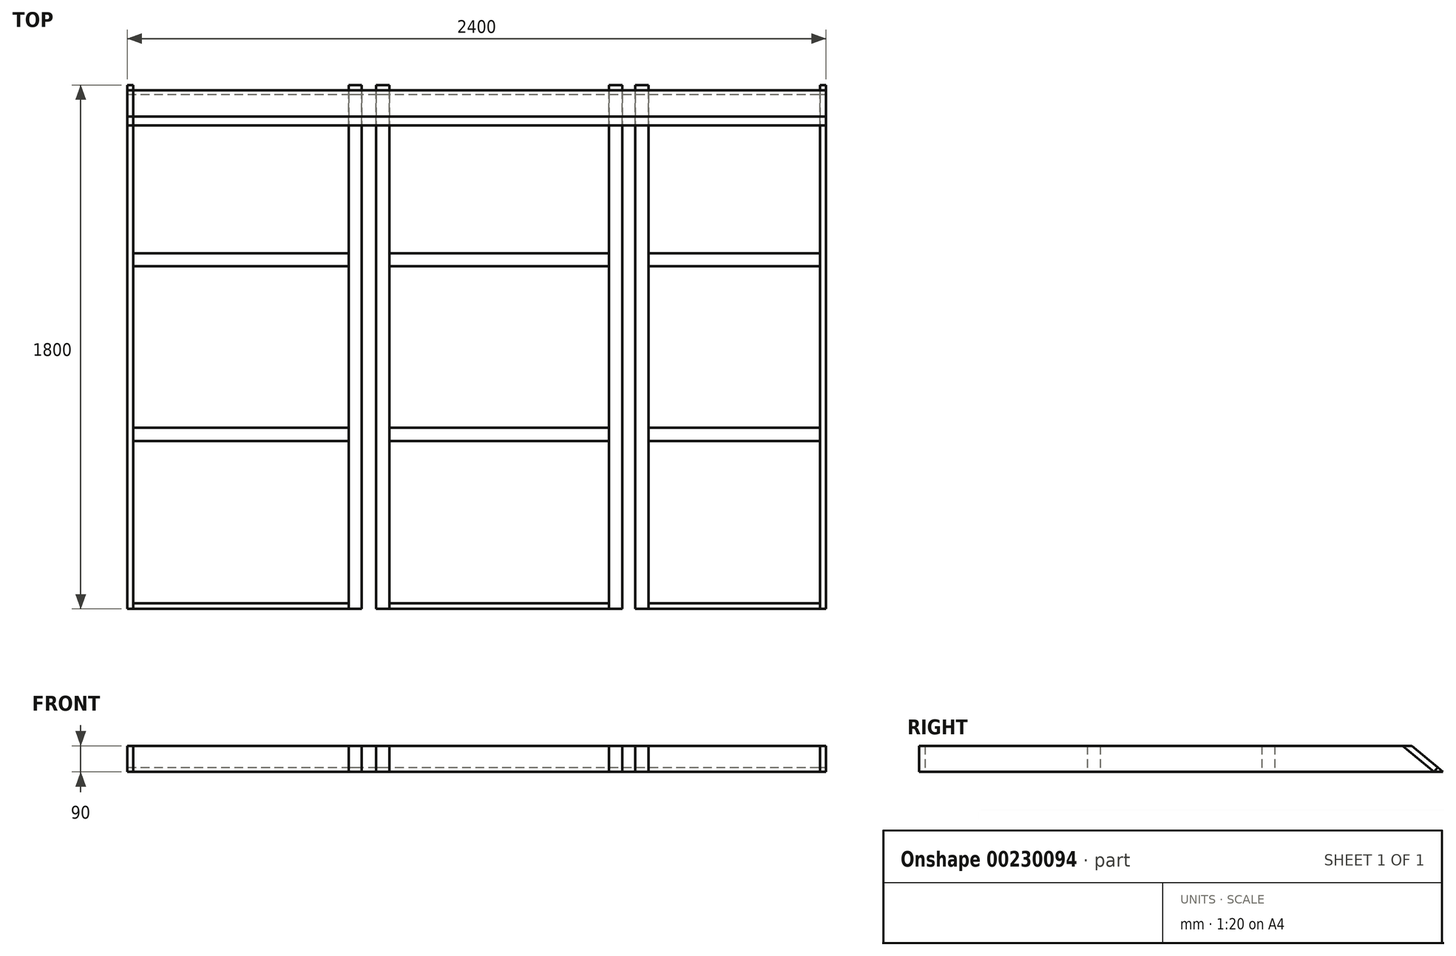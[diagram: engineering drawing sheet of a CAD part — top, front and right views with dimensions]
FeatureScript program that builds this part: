
annotation { "Feature Type Name" : "Feature", "Feature Type Description" : "" }
export const myFeature = defineFeature(function(context is Context, id is Id, definition is map)
    precondition{}
    {
        {
            var Q0;
            Q0=qCreatedBy(makeId("Top.planeOp"),FACE);
            var sketch = newSketch(context, id + "F0", { "sketchPlane" : qUnion([Q0])});
            skLineSegment(sketch, "E0.bottom", {"start": v(1200, 900) * mm, "end": v(-1200, 900) * mm});
            skLineSegment(sketch, "E0.top", {"start": v(1200, -900) * mm, "end": v(-1200, -900) * mm});
            skLineSegment(sketch, "E0.left", {"start": v(1200, 900) * mm, "end": v(1200, -900) * mm});
            skLineSegment(sketch, "E0.right", {"start": v(-1200, 900) * mm, "end": v(-1200, -900) * mm});
            skPoint(sketch, "E0.middle", {"position": v(0, 0) * mm});
            skLineSegment(sketch, "E1", {"start": v(-1180, 900) * mm, "end": v(-1180, -900) * mm});
            skLineSegment(sketch, "E2", {"start": v(-440, 900) * mm, "end": v(-440, -900) * mm});
            skLineSegment(sketch, "E3", {"start": v(-395, 900) * mm, "end": v(-395, -900) * mm});
            skLineSegment(sketch, "E4", {"start": v(-345, 900) * mm, "end": v(-345, -900) * mm});
            skLineSegment(sketch, "E5", {"start": v(-300, 900) * mm, "end": v(-300, -900) * mm});
            skPoint(sketch, "E6.middle", {"position": v(666.84, 0) * mm});
            skLineSegment(sketch, "E7", {"start": v(455, 900) * mm, "end": v(455, -900) * mm});
            skLineSegment(sketch, "E8", {"start": v(500, 900) * mm, "end": v(500, -900) * mm});
            skLineSegment(sketch, "E9", {"start": v(545, 900) * mm, "end": v(545, -900) * mm});
            skLineSegment(sketch, "E10", {"start": v(590, 900) * mm, "end": v(590, -900) * mm});
            skLineSegment(sketch, "E11", {"start": v(1180, 900) * mm, "end": v(1180, -900) * mm});
            skLineSegment(sketch, "E12", {"start": v(-1180, -880) * mm, "end": v(-440, -880) * mm});
            skLineSegment(sketch, "E13", {"start": v(-300, -880) * mm, "end": v(455, -880) * mm});
            skLineSegment(sketch, "E14", {"start": v(590, -880) * mm, "end": v(1180, -880) * mm});
            skLineSegment(sketch, "E15", {"start": v(-1200, 900) * mm, "end": v(-1457.4, 900) * mm});
            skLineSegment(sketch, "E16", {"start": v(-1457.4, 900) * mm, "end": v(-1457.4, 300) * mm});
            skLineSegment(sketch, "E17", {"start": v(-1457.4, 300) * mm, "end": v(-1457.4, -300) * mm});
            skLineSegment(sketch, "E18", {"start": v(-1457.4, -300) * mm, "end": v(-1457.4, -900) * mm});
            skLineSegment(sketch, "E19", {"start": v(-1457.4, 300) * mm, "end": v(1566.79, 300) * mm, "construction": true});
            skLineSegment(sketch, "E20", {"start": v(-1457.4, -300) * mm, "end": v(1566.79, -300) * mm, "construction": true});
            skLineSegment(sketch, "E21", {"start": v(0, 900) * mm, "end": v(0, -1083.47) * mm, "construction": true});
            skLineSegment(sketch, "E22.bottom", {"start": v(1180, 277.5) * mm, "end": v(590, 277.5) * mm});
            skLineSegment(sketch, "E22.top", {"start": v(1180, 322.5) * mm, "end": v(590, 322.5) * mm});
            skLineSegment(sketch, "E22.left", {"start": v(1180, 277.5) * mm, "end": v(1180, 322.5) * mm});
            skLineSegment(sketch, "E22.right", {"start": v(-1180, 277.5) * mm, "end": v(-1180, 322.5) * mm});
            skPoint(sketch, "E22.middle", {"position": v(0, 300) * mm});
            skLineSegment(sketch, "E23.bottom", {"start": v(1180, -322.5) * mm, "end": v(590, -322.5) * mm});
            skLineSegment(sketch, "E23.top", {"start": v(1180, -277.5) * mm, "end": v(590, -277.5) * mm});
            skLineSegment(sketch, "E23.left", {"start": v(1180, -322.5) * mm, "end": v(1180, -277.5) * mm});
            skLineSegment(sketch, "E23.right", {"start": v(-1180, -322.5) * mm, "end": v(-1180, -277.5) * mm});
            skPoint(sketch, "E23.middle", {"position": v(0, -300) * mm});
            skLineSegment(sketch, "E24.trimOffspring", {"start": v(-440, -322.5) * mm, "end": v(-1180, -322.5) * mm});
            skLineSegment(sketch, "E25.trimOffspring", {"start": v(-440, -277.5) * mm, "end": v(-1180, -277.5) * mm});
            skLineSegment(sketch, "E26.trimOffspring", {"start": v(-440, 322.5) * mm, "end": v(-1180, 322.5) * mm});
            skLineSegment(sketch, "E27.trimOffspring", {"start": v(-440, 277.5) * mm, "end": v(-1180, 277.5) * mm});
            skLineSegment(sketch, "E28.trimOffspring", {"start": v(455, 322.5) * mm, "end": v(-300, 322.5) * mm});
            skLineSegment(sketch, "E29.trimOffspring", {"start": v(455, 277.5) * mm, "end": v(-300, 277.5) * mm});
            skLineSegment(sketch, "E30.trimOffspring", {"start": v(455, -277.5) * mm, "end": v(-300, -277.5) * mm});
            skLineSegment(sketch, "E31.trimOffspring", {"start": v(455, -322.5) * mm, "end": v(-300, -322.5) * mm});
            skLineSegment(sketch, "E32", {"start": v(-440, 900) * mm, "end": v(-395, 900) * mm});
            skLineSegment(sketch, "E33", {"start": v(-345, 900) * mm, "end": v(-300, 900) * mm});
            skLineSegment(sketch, "E34", {"start": v(455, 900) * mm, "end": v(500, 900) * mm});
            skLineSegment(sketch, "E35", {"start": v(545, 900) * mm, "end": v(590, 900) * mm});
            skSolve(sketch);
        }
        {
            var Q0;
            {var subQ0=sQuery(id+"F0.wireOp",EDGE,"E0.right");Q0=makeQuery(id+"F0.imprint","IMPRINT",FACE,{"disambiguationData":[TD([[makeQuery(id+"F0.imprint","IMPRINT",EDGE,{"derivedFrom":subQ0}),1.0]])]});}
            var Q1;
            {var subQ6=sQuery(id+"F0.wireOp",EDGE,"E3");Q1=makeQuery(id+"F0.imprint","IMPRINT",FACE,{"disambiguationData":[TD([[makeQuery(id+"F0.imprint","IMPRINT",EDGE,{"derivedFrom":subQ6}),-1.0]])]});}
            var Q2;
            {var subQ4=sQuery(id+"F0.wireOp",EDGE,"E4");Q2=makeQuery(id+"F0.imprint","IMPRINT",FACE,{"disambiguationData":[TD([[makeQuery(id+"F0.imprint","IMPRINT",EDGE,{"derivedFrom":subQ4}),1.0]])]});}
            var Q3;
            {var subQ6=sQuery(id+"F0.wireOp",EDGE,"E8");Q3=makeQuery(id+"F0.imprint","IMPRINT",FACE,{"disambiguationData":[TD([[makeQuery(id+"F0.imprint","IMPRINT",EDGE,{"derivedFrom":subQ6}),-1.0]])]});}
            var Q4;
            {var subQ4=sQuery(id+"F0.wireOp",EDGE,"E9");Q4=makeQuery(id+"F0.imprint","IMPRINT",FACE,{"disambiguationData":[TD([[makeQuery(id+"F0.imprint","IMPRINT",EDGE,{"derivedFrom":subQ4}),1.0]])]});}
            var Q5;
            {var subQ4=sQuery(id+"F0.wireOp",EDGE,"E0.left");Q5=makeQuery(id+"F0.imprint","IMPRINT",FACE,{"disambiguationData":[TD([[makeQuery(id+"F0.imprint","IMPRINT",EDGE,{"derivedFrom":subQ4}),-1.0]])]});}
            extrude(context, id + "F1", {"entities" : qUnion([Q0, Q1, Q2, Q3, Q4, Q5]), "depth" : 90 * mm, "offsetDistance" : 25 * mm});
        }
        {
            var Q0;
            {var subQ5=sQuery(id+"F0.wireOp",EDGE,"E12");Q0=makeQuery(id+"F0.imprint","IMPRINT",FACE,{"disambiguationData":[TD([[makeQuery(id+"F0.imprint","IMPRINT",EDGE,{"derivedFrom":subQ5}),-1.0]])]});}
            var Q1;
            {var subQ5=sQuery(id+"F0.wireOp",EDGE,"E13");Q1=makeQuery(id+"F0.imprint","IMPRINT",FACE,{"disambiguationData":[TD([[makeQuery(id+"F0.imprint","IMPRINT",EDGE,{"derivedFrom":subQ5}),-1.0]])]});}
            var Q2;
            {var subQ5=sQuery(id+"F0.wireOp",EDGE,"E14");Q2=makeQuery(id+"F0.imprint","IMPRINT",FACE,{"disambiguationData":[TD([[makeQuery(id+"F0.imprint","IMPRINT",EDGE,{"derivedFrom":subQ5}),-1.0]])]});}
            extrude(context, id + "F2", {"entities" : qUnion([Q0, Q1, Q2]), "depth" : 90 * mm, "offsetDistance" : 25 * mm});
        }
        {
            var Q0;
            {var subQ0=sQuery(id+"F0.wireOp",EDGE,"E26.trimOffspring");Q0=makeQuery(id+"F0.imprint","IMPRINT",FACE,{"disambiguationData":[TD([[makeQuery(id+"F0.imprint","IMPRINT",EDGE,{"derivedFrom":subQ0}),1.0]])]});}
            var Q1;
            {var subQ0=sQuery(id+"F0.wireOp",EDGE,"E28.trimOffspring");Q1=makeQuery(id+"F0.imprint","IMPRINT",FACE,{"disambiguationData":[TD([[makeQuery(id+"F0.imprint","IMPRINT",EDGE,{"derivedFrom":subQ0}),1.0]])]});}
            var Q2;
            {var subQ0=sQuery(id+"F0.wireOp",EDGE,"E22.bottom");Q2=makeQuery(id+"F0.imprint","IMPRINT",FACE,{"disambiguationData":[TD([[makeQuery(id+"F0.imprint","IMPRINT",EDGE,{"derivedFrom":subQ0}),-1.0]])]});}
            var Q3;
            {var subQ0=sQuery(id+"F0.wireOp",EDGE,"E23.bottom");Q3=makeQuery(id+"F0.imprint","IMPRINT",FACE,{"disambiguationData":[TD([[makeQuery(id+"F0.imprint","IMPRINT",EDGE,{"derivedFrom":subQ0}),-1.0]])]});}
            var Q4;
            {var subQ0=sQuery(id+"F0.wireOp",EDGE,"E24.trimOffspring");Q4=makeQuery(id+"F0.imprint","IMPRINT",FACE,{"disambiguationData":[TD([[makeQuery(id+"F0.imprint","IMPRINT",EDGE,{"derivedFrom":subQ0}),-1.0]])]});}
            var Q5;
            {var subQ0=sQuery(id+"F0.wireOp",EDGE,"E30.trimOffspring");Q5=makeQuery(id+"F0.imprint","IMPRINT",FACE,{"disambiguationData":[TD([[makeQuery(id+"F0.imprint","IMPRINT",EDGE,{"derivedFrom":subQ0}),1.0]])]});}
            extrude(context, id + "F3", {"entities" : qUnion([Q0, Q1, Q2, Q3, Q4, Q5]), "depth" : 90 * mm, "offsetDistance" : 25 * mm});
        }
        {
            var Q0;
            Q0=makeQuery(id+"F1.opExtrude","SWEPT_FACE",FACE,{"disambiguationData":[OSD([sQuery(id+"F0.wireOp",EDGE,"E0.left")])]});
            var sketch = newSketch(context, id + "F4", { "sketchPlane" : qUnion([Q0])});
            skLineSegment(sketch, "E36", {"start": v(900, 0) * mm, "end": v(900, 90) * mm});
            skLineSegment(sketch, "E37", {"start": v(900, 0) * mm, "end": v(792.74, 90) * mm});
            skLineSegment(sketch, "E38", {"start": v(761.63, 90) * mm, "end": v(868.89, 0) * mm});
            skLineSegment(sketch, "E39", {"start": v(792.74, 90) * mm, "end": v(779.89, 74.68) * mm});
            skLineSegment(sketch, "E40", {"start": v(868.89, 0) * mm, "end": v(881.74, 15.32) * mm});
            skLineSegment(sketch, "E41", {"start": v(868.89, 0) * mm, "end": v(798.88, 0) * mm});
            skLineSegment(sketch, "E42", {"start": v(798.88, 0) * mm, "end": v(784.8, 11.8) * mm});
            skLineSegment(sketch, "E43", {"start": v(784.8, 11.8) * mm, "end": v(813.73, 46.28) * mm});
            skLineSegment(sketch, "E44.bottom", {"start": v(971.7, 98.75) * mm, "end": v(1016.7, 98.75) * mm});
            skLineSegment(sketch, "E44.top", {"start": v(971.7, 8.75) * mm, "end": v(1016.7, 8.75) * mm});
            skLineSegment(sketch, "E44.left", {"start": v(971.7, 98.75) * mm, "end": v(971.7, 8.75) * mm});
            skLineSegment(sketch, "E44.right", {"start": v(1016.7, 98.75) * mm, "end": v(1016.7, 8.75) * mm});
            skLineSegment(sketch, "E45", {"start": v(955.44, 99.95) * mm, "end": v(1030.31, 10.72) * mm});
            skLineSegment(sketch, "E46", {"start": v(994.2, 98.75) * mm, "end": v(994.2, 8.75) * mm, "construction": true});
            skLineSegment(sketch, "E47", {"start": v(1016.7, 53.75) * mm, "end": v(971.7, 53.75) * mm, "construction": true});
            skPoint(sketch, "E48", {"position": v(994.2, 53.75) * mm});
            skPoint(sketch, "E49", {"position": v(1016.7, 26.93) * mm});
            skPoint(sketch, "E50", {"position": v(971.7, 80.56) * mm});
            skLineSegment(sketch, "E51", {"start": v(1092.55, 162.61) * mm, "end": v(1326.88, 162.61) * mm});
            skLineSegment(sketch, "E52", {"start": v(1233.6, 162.61) * mm, "end": v(1147.43, 90.3) * mm});
            skLineSegment(sketch, "E53", {"start": v(1164.65, 104.76) * mm, "end": v(1135.73, 139.23) * mm});
            skLineSegment(sketch, "E54", {"start": v(1135.73, 139.23) * mm, "end": v(1204.67, 197.08) * mm});
            skLineSegment(sketch, "E55", {"start": v(1204.67, 197.08) * mm, "end": v(1233.6, 162.61) * mm});
            skLineSegment(sketch, "E56.bottom", {"start": v(1498.29, 50.73) * mm, "end": v(1543.29, 50.73) * mm});
            skLineSegment(sketch, "E56.top", {"start": v(1498.29, 140.73) * mm, "end": v(1543.29, 140.73) * mm});
            skLineSegment(sketch, "E56.left", {"start": v(1498.29, 50.73) * mm, "end": v(1498.29, 140.73) * mm});
            skLineSegment(sketch, "E56.right", {"start": v(1543.29, 50.73) * mm, "end": v(1543.29, 140.73) * mm});
            skLineSegment(sketch, "E57", {"start": v(1558.5, 140.67) * mm, "end": v(1483.63, 51.45) * mm});
            skLineSegment(sketch, "E58", {"start": v(1498.29, 95.73) * mm, "end": v(1543.29, 95.73) * mm});
            skPoint(sketch, "E59", {"position": v(1520.79, 95.73) * mm});
            skLineSegment(sketch, "E60", {"start": v(900, 0) * mm, "end": v(991.3, -76.6) * mm, "construction": true});
            skLineSegment(sketch, "E61", {"start": v(900, 0) * mm, "end": v(869.84, -82.85) * mm, "construction": true});
            skLineSegment(sketch, "E62", {"start": v(900, 0) * mm, "end": v(978.5, -28.57) * mm, "construction": true});
            skSolve(sketch);
        }
        {
            var Q0;
            {var subQ0=sQuery(id+"F4.wireOp",EDGE,"E36");Q0=makeQuery(id+"F4.imprint","IMPRINT",FACE,{"disambiguationData":[TD([[makeQuery(id+"F4.imprint","IMPRINT",EDGE,{"derivedFrom":subQ0}),-1.0]])]});}
            var Q1;
            Q1=makeQuery(id+"F1.opExtrude","SWEPT_FACE",FACE,{"disambiguationData":[OSD([sQuery(id+"F0.wireOp",EDGE,"E0.right")])]});
            extrude(context, id + "F5", {"entities" : qUnion([Q0]), "endBound" : BoundingType.UP_TO_SURFACE, "oppositeDirection" : true, "depth" : 25 * mm, "endBoundEntityFace" : qUnion([Q1]), "offsetDistance" : 25 * mm});
        }
        {
            var Q0;
            Q0=makeQuery(id+"F5.opExtrude","SWEPT_BODY",BODY,{"disambiguationData":[OSD([sQuery(id+"F4.wireOp",EDGE,"9ECzLJ4L-rxAy-AZzF-DnC0-LFDRalDrw8H4"),sQuery(id+"F4.wireOp",EDGE,"sShsUpro-ldYl-YMaO-XyVU-dQZyg97A9EVK"),sQuery(id+"F4.wireOp",EDGE,"E36")])]});
            var Q1;
            Q1=makeQuery(id+"F1.opExtrude","SWEPT_BODY",BODY,{"disambiguationData":[OSD([sQuery(id+"F0.wireOp",EDGE,"E0.bottom"),sQuery(id+"F0.wireOp",EDGE,"E0.top"),sQuery(id+"F0.wireOp",EDGE,"E0.right"),sQuery(id+"F0.wireOp",EDGE,"E1")])]});
            var Q2;
            Q2=makeQuery(id+"F1.opExtrude","SWEPT_BODY",BODY,{"disambiguationData":[OSD([sQuery(id+"F0.wireOp",EDGE,"E0.bottom"),sQuery(id+"F0.wireOp",EDGE,"E0.top"),sQuery(id+"F0.wireOp",EDGE,"E2"),sQuery(id+"F0.wireOp",EDGE,"E3")])]});
            var Q3;
            Q3=makeQuery(id+"F1.opExtrude","SWEPT_BODY",BODY,{"disambiguationData":[OSD([sQuery(id+"F0.wireOp",EDGE,"E0.bottom"),sQuery(id+"F0.wireOp",EDGE,"E0.top"),sQuery(id+"F0.wireOp",EDGE,"E4"),sQuery(id+"F0.wireOp",EDGE,"E5")])]});
            var Q4;
            Q4=makeQuery(id+"F1.opExtrude","SWEPT_BODY",BODY,{"disambiguationData":[OSD([sQuery(id+"F0.wireOp",EDGE,"E0.bottom"),sQuery(id+"F0.wireOp",EDGE,"E0.top"),sQuery(id+"F0.wireOp",EDGE,"E7"),sQuery(id+"F0.wireOp",EDGE,"E8")])]});
            var Q5;
            Q5=makeQuery(id+"F1.opExtrude","SWEPT_BODY",BODY,{"disambiguationData":[OSD([sQuery(id+"F0.wireOp",EDGE,"E0.bottom"),sQuery(id+"F0.wireOp",EDGE,"E0.top"),sQuery(id+"F0.wireOp",EDGE,"E9"),sQuery(id+"F0.wireOp",EDGE,"E10")])]});
            var Q6;
            Q6=makeQuery(id+"F1.opExtrude","SWEPT_BODY",BODY,{"disambiguationData":[OSD([sQuery(id+"F0.wireOp",EDGE,"E0.bottom"),sQuery(id+"F0.wireOp",EDGE,"E0.top"),sQuery(id+"F0.wireOp",EDGE,"E0.left"),sQuery(id+"F0.wireOp",EDGE,"E11")])]});
            booleanBodies(context, id + "F6", {"operationType" : BooleanOperationType.SUBTRACTION, "tools" : qUnion([Q0]), "targets" : qUnion([Q1, Q2, Q3, Q4, Q5, Q6])});
        }
        {
            var Q0;
            {var subQ4=sQuery(id+"F4.wireOp",EDGE,"LHlL5c0t-vV4R-vEGs-6SpN-Y3WtQOfIijEj");Q0=makeQuery(id+"F4.imprint","IMPRINT",FACE,{"disambiguationData":[TD([[makeQuery(id+"F4.imprint","IMPRINT",EDGE,{"derivedFrom":subQ4}),1.0]])]});}
            var Q1;
            {var subQ0=sQuery(id+"F4.wireOp",EDGE,"E39");Q1=makeQuery(id+"F4.imprint","IMPRINT",FACE,{"disambiguationData":[TD([[makeQuery(id+"F4.imprint","IMPRINT",EDGE,{"derivedFrom":subQ0}),1.0]])]});}
            var Q2;
            {var subQ3=sQuery(id+"F4.wireOp",EDGE,"E39");Q2=makeQuery(id+"F4.imprint","IMPRINT",FACE,{"disambiguationData":[TD([[makeQuery(id+"F4.imprint","IMPRINT",EDGE,{"derivedFrom":subQ3}),-1.0]])]});}
            var Q3;
            Q3=makeQuery(id+"F1.opExtrude","SWEPT_FACE",FACE,{"disambiguationData":[OSD([sQuery(id+"F0.wireOp",EDGE,"E0.right")])]});
            extrude(context, id + "F7", {"entities" : qUnion([Q0, Q1, Q2]), "endBound" : BoundingType.UP_TO_SURFACE, "oppositeDirection" : true, "depth" : 25 * mm, "endBoundEntityFace" : qUnion([Q3]), "offsetDistance" : 25 * mm});
        }
        {
            var Q0;
            {var subQ3=sQuery(id+"F4.wireOp",EDGE,"2vfObQFb-Nqpe-k52Z-5iIO-GQCWKJjlV51h");Q0=makeQuery(id+"F4.imprint","IMPRINT",FACE,{"disambiguationData":[TD([[makeQuery(id+"F4.imprint","IMPRINT",EDGE,{"derivedFrom":subQ3}),1.0]])]});}
            var Q1;
            {var subQ0=sQuery(id+"F4.wireOp",EDGE,"E41");Q1=makeQuery(id+"F4.imprint","IMPRINT",FACE,{"disambiguationData":[TD([[makeQuery(id+"F4.imprint","IMPRINT",EDGE,{"derivedFrom":subQ0}),-1.0]])]});}
            var Q2;
            Q2=makeQuery(id+"F1.opExtrude","SWEPT_FACE",FACE,{"disambiguationData":[OSD([sQuery(id+"F0.wireOp",EDGE,"E1")])]});
            extrude(context, id + "F8", {"entities" : qUnion([Q0, Q1]), "endBound" : BoundingType.UP_TO_SURFACE, "oppositeDirection" : true, "depth" : 25 * mm, "endBoundEntityFace" : qUnion([Q2]), "offsetDistance" : 25 * mm});
        }
        {
            var Q0;
            Q0=makeQuery(id+"F1.opExtrude","SWEPT_BODY",BODY,{"disambiguationData":[OSD([sQuery(id+"F0.wireOp",EDGE,"E0.bottom"),sQuery(id+"F0.wireOp",EDGE,"E0.top"),sQuery(id+"F0.wireOp",EDGE,"E9"),sQuery(id+"F0.wireOp",EDGE,"E10")])]});
            var Q1;
            Q1=makeQuery(id+"F1.opExtrude","SWEPT_BODY",BODY,{"disambiguationData":[OSD([sQuery(id+"F0.wireOp",EDGE,"E0.bottom"),sQuery(id+"F0.wireOp",EDGE,"E0.top"),sQuery(id+"F0.wireOp",EDGE,"E7"),sQuery(id+"F0.wireOp",EDGE,"E8")])]});
            var Q2;
            Q2=makeQuery(id+"F1.opExtrude","SWEPT_BODY",BODY,{"disambiguationData":[OSD([sQuery(id+"F0.wireOp",EDGE,"E0.bottom"),sQuery(id+"F0.wireOp",EDGE,"E0.top"),sQuery(id+"F0.wireOp",EDGE,"E0.left"),sQuery(id+"F0.wireOp",EDGE,"E11")])]});
            var Q3;
            Q3=makeQuery(id+"F1.opExtrude","SWEPT_BODY",BODY,{"disambiguationData":[OSD([sQuery(id+"F0.wireOp",EDGE,"E0.bottom"),sQuery(id+"F0.wireOp",EDGE,"E0.top"),sQuery(id+"F0.wireOp",EDGE,"E4"),sQuery(id+"F0.wireOp",EDGE,"E5")])]});
            var Q4;
            Q4=makeQuery(id+"F1.opExtrude","SWEPT_BODY",BODY,{"disambiguationData":[OSD([sQuery(id+"F0.wireOp",EDGE,"E0.bottom"),sQuery(id+"F0.wireOp",EDGE,"E0.top"),sQuery(id+"F0.wireOp",EDGE,"E2"),sQuery(id+"F0.wireOp",EDGE,"E3")])]});
            var Q5;
            Q5=makeQuery(id+"F8.opExtrude","SWEPT_BODY",BODY,{"disambiguationData":[OSD([sQuery(id+"F4.wireOp",EDGE,"E38"),sQuery(id+"F4.wireOp",EDGE,"E41"),sQuery(id+"F4.wireOp",EDGE,"E42"),sQuery(id+"F4.wireOp",EDGE,"E43")])]});
            booleanBodies(context, id + "F9", {"operationType" : BooleanOperationType.SUBTRACTION, "tools" : qUnion([Q0, Q1, Q2, Q3, Q4]), "targets" : qUnion([Q5]), "keepTools" : true});
        }
        {
            var Q0;
            Q0=makeQuery(id+"F9.opBoolean","SPLIT",BODY,{"disambiguationData":[OD(3.0)],"derivedFrom":makeQuery(id+"F8.opExtrude","SWEPT_BODY",BODY,{"disambiguationData":[OSD([sQuery(id+"F4.wireOp",EDGE,"E38"),sQuery(id+"F4.wireOp",EDGE,"E41"),sQuery(id+"F4.wireOp",EDGE,"E42"),sQuery(id+"F4.wireOp",EDGE,"E43")])]})});
            var Q1;
            Q1=makeQuery(id+"F9.opBoolean","SPLIT",BODY,{"disambiguationData":[OD(1.0)],"derivedFrom":makeQuery(id+"F8.opExtrude","SWEPT_BODY",BODY,{"disambiguationData":[OSD([sQuery(id+"F4.wireOp",EDGE,"E38"),sQuery(id+"F4.wireOp",EDGE,"E41"),sQuery(id+"F4.wireOp",EDGE,"E42"),sQuery(id+"F4.wireOp",EDGE,"E43")])]})});
            deleteBodies(context, id + "F10", {"entities" : qUnion([Q0, Q1])});
        }
        {
            var Q0;
            Q0=makeQuery(id+"F7.opExtrude","SWEPT_BODY",BODY,{"disambiguationData":[OSD([sQuery(id+"F0.wireOp",EDGE,"E0.left"),sQuery(id+"F4.wireOp",EDGE,"E37"),sQuery(id+"F4.wireOp",EDGE,"E38"),sQuery(id+"F4.wireOp",EDGE,"E40")])]});
            var Q1;
            Q1=makeQuery(id+"F1.opExtrude","SWEPT_BODY",BODY,{"disambiguationData":[OSD([sQuery(id+"F0.wireOp",EDGE,"E0.bottom"),sQuery(id+"F0.wireOp",EDGE,"E0.top"),sQuery(id+"F0.wireOp",EDGE,"E2"),sQuery(id+"F0.wireOp",EDGE,"E3")])]});
            var Q2;
            Q2=makeQuery(id+"F1.opExtrude","SWEPT_BODY",BODY,{"disambiguationData":[OSD([sQuery(id+"F0.wireOp",EDGE,"E0.bottom"),sQuery(id+"F0.wireOp",EDGE,"E0.top"),sQuery(id+"F0.wireOp",EDGE,"E4"),sQuery(id+"F0.wireOp",EDGE,"E5")])]});
            var Q3;
            Q3=makeQuery(id+"F1.opExtrude","SWEPT_BODY",BODY,{"disambiguationData":[OSD([sQuery(id+"F0.wireOp",EDGE,"E0.bottom"),sQuery(id+"F0.wireOp",EDGE,"E0.top"),sQuery(id+"F0.wireOp",EDGE,"E7"),sQuery(id+"F0.wireOp",EDGE,"E8")])]});
            var Q4;
            Q4=makeQuery(id+"F1.opExtrude","SWEPT_BODY",BODY,{"disambiguationData":[OSD([sQuery(id+"F0.wireOp",EDGE,"E0.bottom"),sQuery(id+"F0.wireOp",EDGE,"E0.top"),sQuery(id+"F0.wireOp",EDGE,"E9"),sQuery(id+"F0.wireOp",EDGE,"E10")])]});
            var Q5;
            Q5=makeQuery(id+"F1.opExtrude","SWEPT_BODY",BODY,{"disambiguationData":[OSD([sQuery(id+"F0.wireOp",EDGE,"E0.bottom"),sQuery(id+"F0.wireOp",EDGE,"E0.top"),sQuery(id+"F0.wireOp",EDGE,"E0.left"),sQuery(id+"F0.wireOp",EDGE,"E11")])]});
            booleanBodies(context, id + "F11", {"operationType" : BooleanOperationType.SUBTRACTION, "tools" : qUnion([Q0]), "targets" : qUnion([Q1, Q2, Q3, Q4, Q5]), "keepTools" : true});
        }
    });
